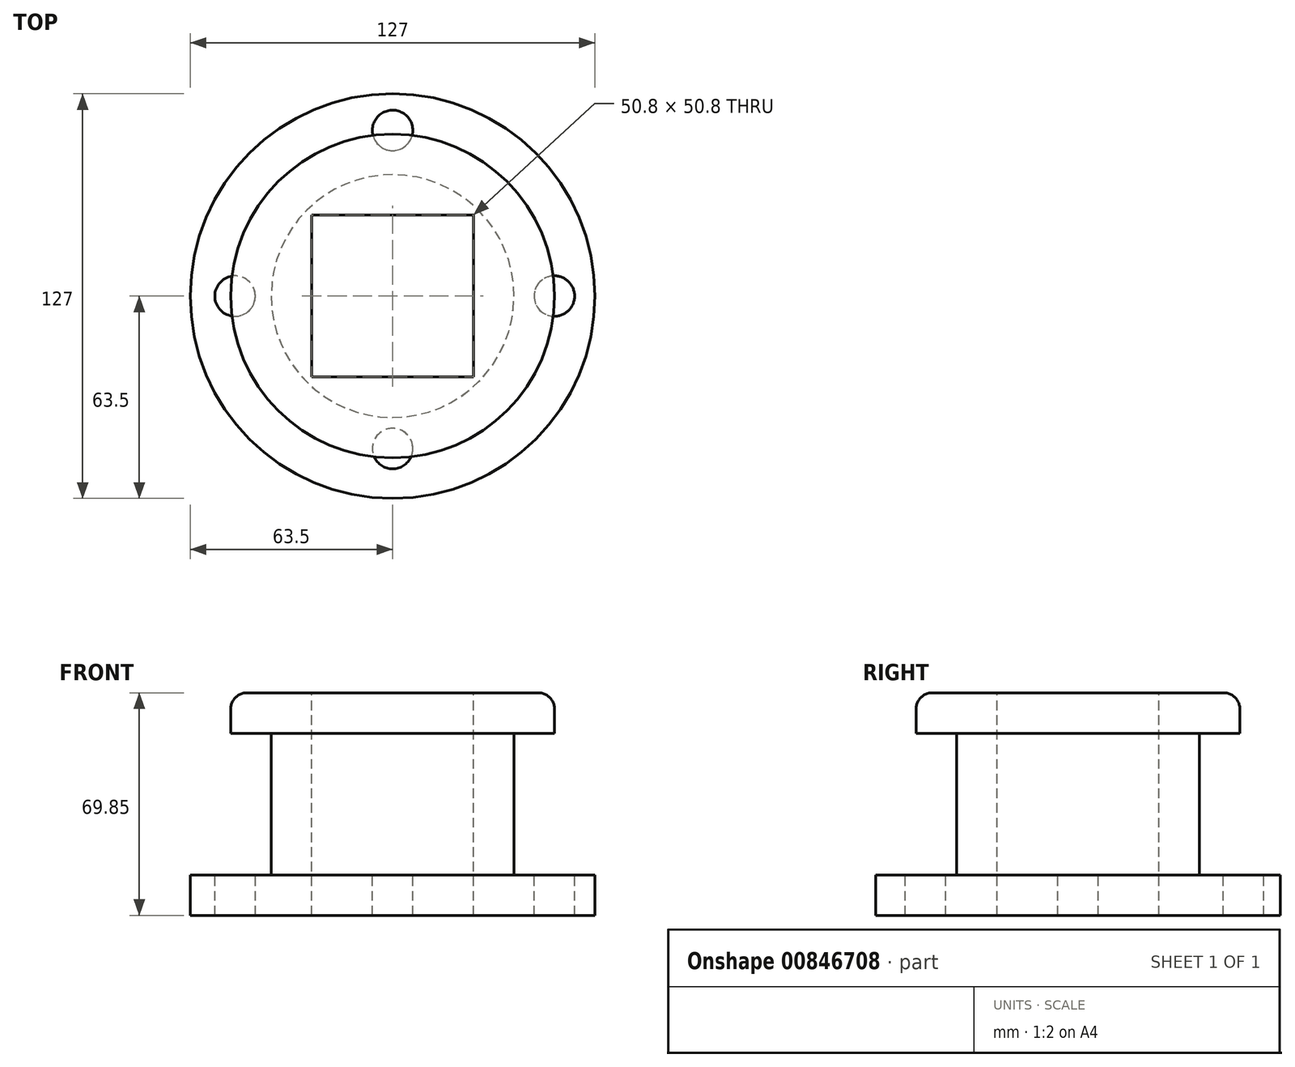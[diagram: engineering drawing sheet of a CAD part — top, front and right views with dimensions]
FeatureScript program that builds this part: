
annotation { "Feature Type Name" : "Feature", "Feature Type Description" : "" }
export const myFeature = defineFeature(function(context is Context, id is Id, definition is map)
    precondition{}
    {
        {
            var Q0;
            Q0=qCreatedBy(makeId("Top.planeOp"),FACE);
            var sketch = newSketch(context, id + "F0", { "sketchPlane" : qUnion([Q0])});
            skCircle(sketch, "E0", {"center": v(0, 0) * mm, "radius": 63.5 * mm});
            skSolve(sketch);
        }
        {
            var Q0;
            Q0 = qSketchRegion(id + "F0", true);
            var Q1;
            Q1=makeQuery(id+"F0.imprint","IMPRINT",FACE,{"disambiguationData":[TD([[makeQuery(id+"F0.imprint","IMPRINT",EDGE,{"derivedFrom":sQuery(id+"F0.wireOp",EDGE,"E0")}),1.0]])]});
            extrude(context, id + "F1", {"entities" : qUnion([Q0, Q1]), "depth" : 12.7 * mm, "offsetDistance" : 25.4 * mm});
        }
        {
            var Q0;
            Q0=makeQuery(id+"F1.opExtrude","CAP_FACE",FACE,{"disambiguationData":[OSD([sQuery(id+"F0.wireOp",EDGE,"E0")])],"isStart":true});
            var sketch = newSketch(context, id + "F2", { "sketchPlane" : qUnion([Q0])});
            skCircle(sketch, "E1", {"center": v(0, 0) * mm, "radius": 38.1 * mm});
            skSolve(sketch);
        }
        {
            var Q0;
            Q0 = qSketchRegion(id + "F2", true);
            extrude(context, id + "F3", {"entities" : qUnion([Q0]), "operationType" : NewBodyOperationType.ADD, "oppositeDirection" : true, "depth" : 57.15 * mm, "offsetDistance" : 25.4 * mm});
        }
        {
            var Q0;
            Q0=makeQuery(id+"F3.opExtrude","CAP_FACE",FACE,{"disambiguationData":[OSD([sQuery(id+"F2.wireOp",EDGE,"E1")])],"isStart":false});
            var sketch = newSketch(context, id + "F4", { "sketchPlane" : qUnion([Q0])});
            skCircle(sketch, "E2", {"center": v(0, 0) * mm, "radius": 50.8 * mm});
            skSolve(sketch);
        }
        {
            var Q0;
            Q0 = qSketchRegion(id + "F4", true);
            extrude(context, id + "F5", {"entities" : qUnion([Q0]), "operationType" : NewBodyOperationType.ADD, "depth" : 12.7 * mm, "offsetDistance" : 25.4 * mm});
        }
        {
            var Q0;
            Q0=makeQuery(id+"F5.opExtrude","CAP_FACE",FACE,{"disambiguationData":[OSD([sQuery(id+"F4.wireOp",EDGE,"E2")])],"isStart":false});
            fillet(context, id + "F6", {"entities" : qUnion([Q0]), "radius" : 5.08 * mm, "tangentPropagation" : true, "allowEdgeOverflow" : false});
        }
        {
            var Q0;
            Q0=makeQuery(id+"F5.opExtrude","CAP_FACE",FACE,{"disambiguationData":[OSD([sQuery(id+"F4.wireOp",EDGE,"E2")])],"isStart":false});
            var sketch = newSketch(context, id + "F7", { "sketchPlane" : qUnion([Q0])});
            skPoint(sketch, "E3.bottom.start.orphan", {"position": v(0, 0) * mm});
            skLineSegment(sketch, "E4.bottom", {"start": v(25.4, -25.4) * mm, "end": v(-25.4, -25.4) * mm});
            skLineSegment(sketch, "E4.top", {"start": v(25.4, 25.4) * mm, "end": v(-25.4, 25.4) * mm});
            skLineSegment(sketch, "E4.left", {"start": v(25.4, -25.4) * mm, "end": v(25.4, 25.4) * mm});
            skLineSegment(sketch, "E4.right", {"start": v(-25.4, -25.4) * mm, "end": v(-25.4, 25.4) * mm});
            skSolve(sketch);
        }
        {
            var Q0;
            Q0=makeQuery(id+"F1.opExtrude","CAP_FACE",FACE,{"disambiguationData":[OSD([sQuery(id+"F0.wireOp",EDGE,"E0")])],"isStart":false});
            var sketch = newSketch(context, id + "F8", { "sketchPlane" : qUnion([Q0])});
            skPoint(sketch, "E5.center.orphan", {"position": v(-56.5, 0) * mm});
            skPoint(sketch, "E6.center.orphan", {"position": v(0, -55.83) * mm});
            skPoint(sketch, "E7.center.orphan", {"position": v(55.66, 0) * mm});
            skPoint(sketch, "E8.center.orphan", {"position": v(0, 56.5) * mm});
            skCircle(sketch, "E9", {"center": v(-49.44, 0) * mm, "radius": 6.35 * mm});
            skCircle(sketch, "E10", {"center": v(0, -47.86) * mm, "radius": 6.35 * mm});
            skCircle(sketch, "E11", {"center": v(50.77, 0) * mm, "radius": 6.35 * mm});
            skCircle(sketch, "E12", {"center": v(0, 52) * mm, "radius": 6.35 * mm});
            skSolve(sketch);
        }
        {
            var Q0;
            Q0 = qSketchRegion(id + "F8", true);
            extrude(context, id + "F9", {"entities" : qUnion([Q0]), "operationType" : NewBodyOperationType.REMOVE, "oppositeDirection" : true, "depth" : 25.4 * mm, "offsetDistance" : 25.4 * mm});
        }
        {
            var Q0;
            Q0 = qSketchRegion(id + "F8", true);
            extrude(context, id + "F10", {"entities" : qUnion([Q0]), "operationType" : NewBodyOperationType.REMOVE, "oppositeDirection" : true, "depth" : 25.4 * mm, "offsetDistance" : 25.4 * mm});
        }
        {
            var Q0;
            Q0 = qSketchRegion(id + "F7", true);
            extrude(context, id + "F11", {"entities" : qUnion([Q0]), "operationType" : NewBodyOperationType.REMOVE, "oppositeDirection" : true, "depth" : 127 * mm, "offsetDistance" : 25.4 * mm});
        }
    });
